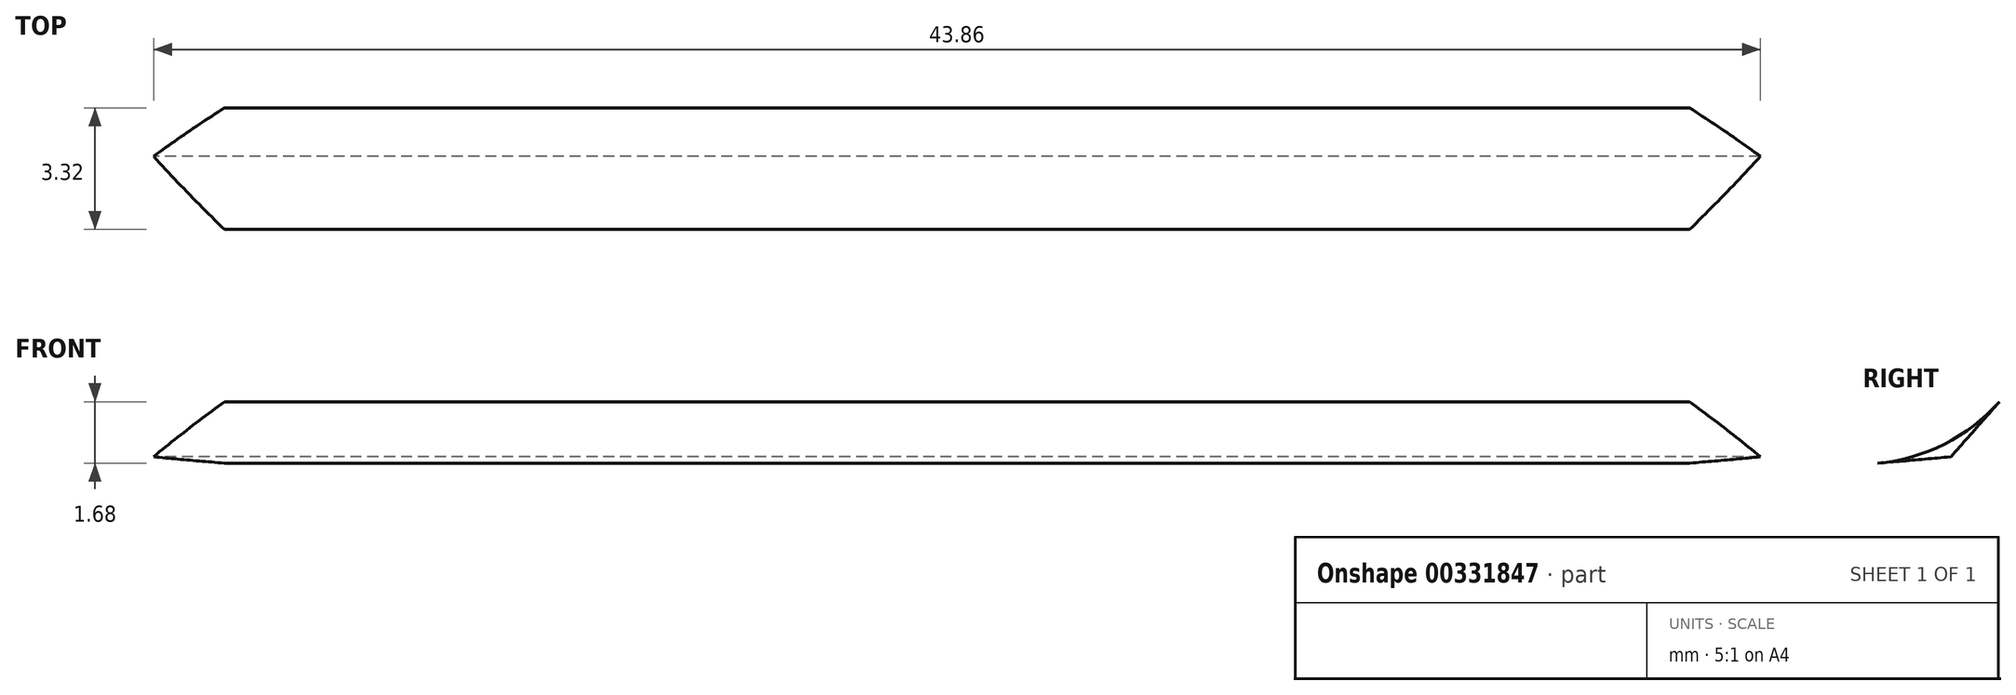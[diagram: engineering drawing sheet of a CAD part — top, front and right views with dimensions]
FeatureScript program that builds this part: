
annotation { "Feature Type Name" : "Feature", "Feature Type Description" : "" }
export const myFeature = defineFeature(function(context is Context, id is Id, definition is map)
    precondition{}
    {
        {
            var Q0;
            Q0=qCreatedBy(makeId("Right.planeOp"),FACE);
            var sketch = newSketch(context, id + "F0", { "sketchPlane" : qUnion([Q0])});
            skLineSegment(sketch, "E0.bottom", {"start": v(-61.46, 0) * mm, "end": v(71.54, 0) * mm});
            skLineSegment(sketch, "E0.top", {"start": v(-61.46, 55.25) * mm, "end": v(71.54, 55.25) * mm});
            skLineSegment(sketch, "E0.left", {"start": v(-61.46, 0) * mm, "end": v(-61.46, 55.25) * mm});
            skLineSegment(sketch, "E0.right", {"start": v(71.54, 0) * mm, "end": v(71.54, 55.25) * mm});
            skCircle(sketch, "E1", {"center": v(-29.68, 0) * mm, "radius": 12 * mm});
            skCircle(sketch, "E2", {"center": v(41.54, 2) * mm, "radius": 12 * mm});
            skLineSegment(sketch, "E3", {"start": v(-61.46, 27.62) * mm, "end": v(0, 32.97) * mm});
            skLineSegment(sketch, "E4", {"start": v(0, 32.97) * mm, "end": v(19.6, 55.25) * mm});
            skLineSegment(sketch, "E5", {"start": v(49.85, 55.25) * mm, "end": v(71.54, 36.47) * mm});
            skSolve(sketch);
        }
        {
            var Q0;
            {var subQ0=sQuery(id+"F0.wireOp",EDGE,"E3");Q0=makeQuery(id+"F0.imprint","IMPRINT",FACE,{"disambiguationData":[TD([[makeQuery(id+"F0.imprint","IMPRINT",EDGE,{"derivedFrom":subQ0}),-1.0]])]});}
            var Q1;
            {var subQ0=sQuery(id+"F0.wireOp",EDGE,"E1");var subQ1=sQuery(id+"F0.wireOp",EDGE,"E0.bottom");var subQ2=makeQuery(id+"F0.imprint","INTERSECT",VERTEX,{"disambiguationData":[OD(0.0)],"derivedFrom":[subQ1,subQ0]});Q1=makeQuery(id+"F0.imprint","IMPRINT",FACE,{"disambiguationData":[TD([[makeQuery(id+"F0.imprint","IMPRINT",EDGE,{"disambiguationData":[TD([[subQ2,-1.0]])],"derivedFrom":subQ1}),1.0]])]});}
            var Q2;
            {var subQ0=sQuery(id+"F0.wireOp",EDGE,"E2");var subQ1=sQuery(id+"F0.wireOp",EDGE,"E0.bottom");var subQ2=makeQuery(id+"F0.imprint","INTERSECT",VERTEX,{"disambiguationData":[OD(0.0)],"derivedFrom":[subQ1,subQ0]});Q2=makeQuery(id+"F0.imprint","IMPRINT",FACE,{"disambiguationData":[TD([[makeQuery(id+"F0.imprint","IMPRINT",EDGE,{"disambiguationData":[TD([[subQ2,-1.0]])],"derivedFrom":subQ1}),1.0]])]});}
            extrude(context, id + "F1", {"entities" : qUnion([Q0, Q1, Q2]), "depth" : 25 * mm});
        }
        {
            var Q0;
            Q0=makeQuery(id+"F1.opExtrude","CAP_FACE",FACE,{"disambiguationData":[OSD([sQuery(id+"F0.wireOp",EDGE,"E0.bottom"),sQuery(id+"F0.wireOp",EDGE,"E0.top"),sQuery(id+"F0.wireOp",EDGE,"E0.left"),sQuery(id+"F0.wireOp",EDGE,"E0.right"),sQuery(id+"F0.wireOp",EDGE,"E3"),sQuery(id+"F0.wireOp",EDGE,"E4"),sQuery(id+"F0.wireOp",EDGE,"E5")])],"isStart":true});
            extrude(context, id + "F2", {"entities" : qUnion([Q0]), "operationType" : NewBodyOperationType.ADD, "depth" : 25 * mm});
        }
        {
            var Q0;
            {var subQ0=sQuery(id+"F0.wireOp",EDGE,"E0.bottom");Q0=makeQuery(id+"F2.boolean.opBoolean","MERGE",FACE,{"derivedFrom":[makeQuery(id+"F1.opExtrude","SWEPT_FACE",FACE,{"disambiguationData":[OSD([subQ0])]}),makeQuery(id+"F2.opExtrude","SWEPT_FACE",FACE,{"disambiguationData":[OSD([subQ0])]})]});}
            shell(context, id + "F3", {"entities" : qUnion([Q0]), "thickness" : 2.5 * mm});
        }
        {
            var Q0;
            Q0=makeQuery(id+"F2.opExtrude","CAP_EDGE",EDGE,{"disambiguationData":[OSD([sQuery(id+"F0.wireOp",EDGE,"E0.left")])],"isStart":false});
            var Q1;
            {var subQ0=sQuery(id+"F0.wireOp",EDGE,"E3");var subQ1=sQuery(id+"F0.wireOp",EDGE,"E0.left");Q1=makeQuery(id+"F2.boolean.opBoolean","MERGE",EDGE,{"derivedFrom":[makeQuery(id+"F1.opExtrude","SWEPT_EDGE",EDGE,{"disambiguationData":[OSD([subQ1,subQ0])]}),makeQuery(id+"F2.opExtrude","SWEPT_EDGE",EDGE,{"disambiguationData":[OSD([subQ1,subQ0])]})]});}
            var Q2;
            Q2=makeQuery(id+"F1.opExtrude","CAP_EDGE",EDGE,{"disambiguationData":[OSD([sQuery(id+"F0.wireOp",EDGE,"E0.left")])],"isStart":false});
            var Q3;
            Q3=makeQuery(id+"F1.opExtrude","CAP_EDGE",EDGE,{"disambiguationData":[OSD([sQuery(id+"F0.wireOp",EDGE,"E3")])],"isStart":false});
            var Q4;
            Q4=makeQuery(id+"F2.opExtrude","CAP_EDGE",EDGE,{"disambiguationData":[OSD([sQuery(id+"F0.wireOp",EDGE,"E3")])],"isStart":false});
            var Q5;
            {var subQ0=sQuery(id+"F0.wireOp",EDGE,"E5");var subQ1=sQuery(id+"F0.wireOp",EDGE,"E0.right");Q5=makeQuery(id+"F2.boolean.opBoolean","MERGE",EDGE,{"derivedFrom":[makeQuery(id+"F1.opExtrude","SWEPT_EDGE",EDGE,{"disambiguationData":[OSD([subQ1,subQ0])]}),makeQuery(id+"F2.opExtrude","SWEPT_EDGE",EDGE,{"disambiguationData":[OSD([subQ1,subQ0])]})]});}
            var Q6;
            Q6=makeQuery(id+"F1.opExtrude","CAP_EDGE",EDGE,{"disambiguationData":[OSD([sQuery(id+"F0.wireOp",EDGE,"E0.top")])],"isStart":false});
            var Q7;
            {var subQ0=sQuery(id+"F0.wireOp",EDGE,"E4");Q7=makeQuery(id+"F2.boolean.opBoolean","MERGE",FACE,{"derivedFrom":[makeQuery(id+"F1.opExtrude","SWEPT_FACE",FACE,{"disambiguationData":[OSD([subQ0])]}),makeQuery(id+"F2.opExtrude","SWEPT_FACE",FACE,{"disambiguationData":[OSD([subQ0])]})]});}
            var Q8;
            Q8=makeQuery(id+"F2.opExtrude","CAP_EDGE",EDGE,{"disambiguationData":[OSD([sQuery(id+"F0.wireOp",EDGE,"E0.top")])],"isStart":false});
            var Q9;
            {var subQ0=sQuery(id+"F0.wireOp",EDGE,"E0.top");Q9=makeQuery(id+"F2.boolean.opBoolean","MERGE",FACE,{"derivedFrom":[makeQuery(id+"F1.opExtrude","SWEPT_FACE",FACE,{"disambiguationData":[OSD([subQ0])]}),makeQuery(id+"F2.opExtrude","SWEPT_FACE",FACE,{"disambiguationData":[OSD([subQ0])]})]});}
            var Q10;
            Q10=makeQuery(id+"F2.opExtrude","CAP_EDGE",EDGE,{"disambiguationData":[OSD([sQuery(id+"F0.wireOp",EDGE,"E0.right")])],"isStart":false});
            var Q11;
            Q11=makeQuery(id+"F1.opExtrude","CAP_EDGE",EDGE,{"disambiguationData":[OSD([sQuery(id+"F0.wireOp",EDGE,"E0.right")])],"isStart":false});
            var Q12;
            Q12=makeQuery(id+"F1.opExtrude","CAP_EDGE",EDGE,{"disambiguationData":[OSD([sQuery(id+"F0.wireOp",EDGE,"E5")])],"isStart":false});
            var Q13;
            Q13=makeQuery(id+"F2.opExtrude","CAP_EDGE",EDGE,{"disambiguationData":[OSD([sQuery(id+"F0.wireOp",EDGE,"E5")])],"isStart":false});
            fillet(context, id + "F4", {"entities" : qUnion([Q0, Q1, Q2, Q3, Q4, Q5, Q6, Q7, Q8, Q9, Q10, Q11, Q12, Q13]), "radius" : 5 * mm, "tangentPropagation" : true, "allowEdgeOverflow" : false});
        }
        {
            var Q0;
            {var subQ0=sQuery(id+"F0.wireOp",EDGE,"E2");var subQ1=sQuery(id+"F0.wireOp",EDGE,"E0.bottom");var subQ2=makeQuery(id+"F0.imprint","INTERSECT",VERTEX,{"disambiguationData":[OD(0.0)],"derivedFrom":[subQ1,subQ0]});Q0=makeQuery(id+"F0.imprint","IMPRINT",FACE,{"disambiguationData":[TD([[makeQuery(id+"F0.imprint","IMPRINT",EDGE,{"disambiguationData":[TD([[subQ2,-1.0]])],"derivedFrom":subQ1}),1.0]])]});}
            var Q1;
            {var subQ0=sQuery(id+"F0.wireOp",EDGE,"E1");var subQ1=sQuery(id+"F0.wireOp",EDGE,"E0.bottom");var subQ2=makeQuery(id+"F0.imprint","INTERSECT",VERTEX,{"disambiguationData":[OD(0.0)],"derivedFrom":[subQ1,subQ0]});Q1=makeQuery(id+"F0.imprint","IMPRINT",FACE,{"disambiguationData":[TD([[makeQuery(id+"F0.imprint","IMPRINT",EDGE,{"disambiguationData":[TD([[subQ2,-1.0]])],"derivedFrom":subQ1}),1.0]])]});}
            extrude(context, id + "F5", {"entities" : qUnion([Q0, Q1]), "operationType" : NewBodyOperationType.REMOVE, "endBound" : BoundingType.SYMMETRIC, "depth" : 100 * mm});
        }
    });
